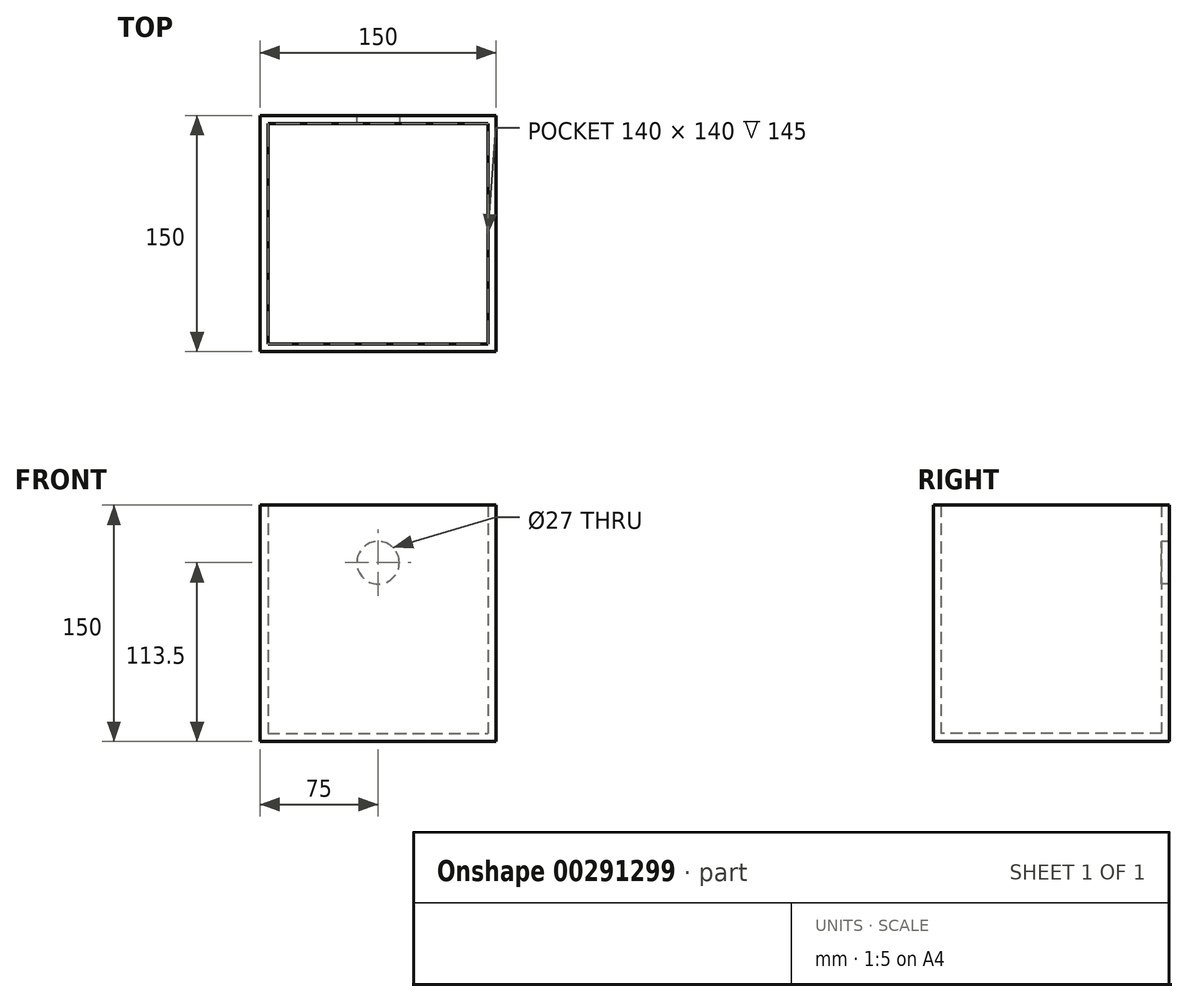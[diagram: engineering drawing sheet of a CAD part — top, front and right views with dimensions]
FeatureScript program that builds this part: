
annotation { "Feature Type Name" : "Feature", "Feature Type Description" : "" }
export const myFeature = defineFeature(function(context is Context, id is Id, definition is map)
    precondition{}
    {
        {
            var Q0;
            Q0=qCreatedBy(makeId("Top.planeOp"),FACE);
            var sketch = newSketch(context, id + "F0", { "sketchPlane" : qUnion([Q0])});
            skLineSegment(sketch, "E0.bottom", {"start": v(-75, 75) * mm, "end": v(75, 75) * mm});
            skLineSegment(sketch, "E0.top", {"start": v(-75, -75) * mm, "end": v(75, -75) * mm});
            skLineSegment(sketch, "E0.left", {"start": v(-75, 75) * mm, "end": v(-75, -75) * mm});
            skLineSegment(sketch, "E0.right", {"start": v(75, 75) * mm, "end": v(75, -75) * mm});
            skPoint(sketch, "E0.middle", {"position": v(0, 0) * mm});
            skSolve(sketch);
        }
        {
            var Q0;
            Q0=makeQuery(id+"F0.imprint","IMPRINT",FACE,{"disambiguationData":[TD([[makeQuery(id+"F0.imprint","IMPRINT",EDGE,{"derivedFrom":sQuery(id+"F0.wireOp",EDGE,"E0.bottom")}),-1.0]])]});
            extrude(context, id + "F1", {"entities" : qUnion([Q0]), "depth" : 150 * mm});
        }
        {
            var Q0;
            Q0=makeQuery(id+"F1.opExtrude","CAP_FACE",FACE,{"disambiguationData":[OSD([sQuery(id+"F0.wireOp",EDGE,"E0.bottom"),sQuery(id+"F0.wireOp",EDGE,"E0.top"),sQuery(id+"F0.wireOp",EDGE,"E0.left"),sQuery(id+"F0.wireOp",EDGE,"E0.right")])],"isStart":false});
            shell(context, id + "F2", {"entities" : qUnion([Q0]), "thickness" : 5 * mm});
        }
        {
            var Q0;
            Q0=makeQuery(id+"F2.opShell","OFFSET_FACE",FACE,{"disambiguationData":[OSD([sQuery(id+"F0.wireOp",EDGE,"E0.bottom")])]});
            var sketch = newSketch(context, id + "F3", { "sketchPlane" : qUnion([Q0])});
            skPoint(sketch, "E1.0", {"position": v(0, 150) * mm});
            skLineSegment(sketch, "E2", {"start": v(0, 150) * mm, "end": v(0, 100) * mm});
            skCircle(sketch, "E3", {"center": v(0, 113.5) * mm, "radius": 13.5 * mm});
            skSolve(sketch);
        }
        {
            var Q0;
            {var subQ0=sQuery(id+"F3.wireOp",EDGE,"E3");var subQ1=sQuery(id+"F3.wireOp",EDGE,"E2");var subQ2=makeQuery(id+"F3.imprint","INTERSECT",VERTEX,{"disambiguationData":[OD(0.0)],"derivedFrom":[subQ1,subQ0]});Q0=makeQuery(id+"F3.imprint","IMPRINT",FACE,{"disambiguationData":[TD([[makeQuery(id+"F3.imprint","IMPRINT",EDGE,{"disambiguationData":[TD([[subQ2,1.0]])],"derivedFrom":subQ1}),1.0]])]});}
            var Q1;
            {var subQ0=sQuery(id+"F3.wireOp",EDGE,"E3");var subQ1=sQuery(id+"F3.wireOp",EDGE,"E2");var subQ2=makeQuery(id+"F3.imprint","INTERSECT",VERTEX,{"disambiguationData":[OD(0.0)],"derivedFrom":[subQ1,subQ0]});Q1=makeQuery(id+"F3.imprint","IMPRINT",FACE,{"disambiguationData":[TD([[makeQuery(id+"F3.imprint","IMPRINT",EDGE,{"disambiguationData":[TD([[subQ2,1.0]])],"derivedFrom":subQ1}),-1.0]])]});}
            var Q2;
            Q2=sQuery(id+"F3.wireOp",EDGE,"E3");
            extrude(context, id + "F4", {"entities" : qUnion([Q0, Q1]), "operationType" : NewBodyOperationType.REMOVE, "surfaceEntities" : qUnion([Q2]), "oppositeDirection" : true, "depth" : 5 * mm});
        }
    });
